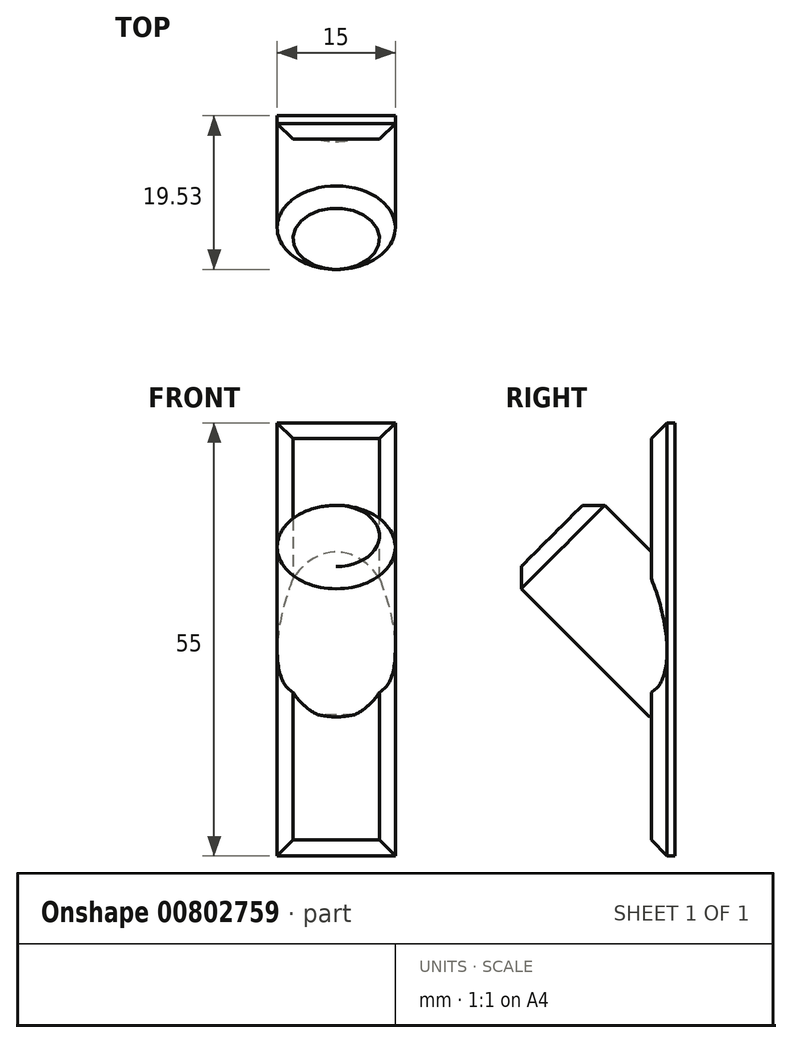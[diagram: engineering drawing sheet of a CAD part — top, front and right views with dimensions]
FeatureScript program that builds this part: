
annotation { "Feature Type Name" : "Feature", "Feature Type Description" : "" }
export const myFeature = defineFeature(function(context is Context, id is Id, definition is map)
    precondition{}
    {
        {
            var Q0;
            Q0=qCreatedBy(makeId("Front.planeOp"),FACE);
            var sketch = newSketch(context, id + "F0", { "sketchPlane" : qUnion([Q0])});
            skLineSegment(sketch, "E0.bottom", {"start": v(-7.5, 30) * mm, "end": v(7.5, 30) * mm});
            skLineSegment(sketch, "E0.top", {"start": v(-7.5, -25) * mm, "end": v(7.5, -25) * mm});
            skLineSegment(sketch, "E0.left", {"start": v(-7.5, 30) * mm, "end": v(-7.5, -25) * mm});
            skLineSegment(sketch, "E0.right", {"start": v(7.5, 30) * mm, "end": v(7.5, -25) * mm});
            skSolve(sketch);
        }
        {
            var Q0;
            Q0=qSketchRegion(id+"F0",true);
            extrude(context, id + "F1", {"entities" : qUnion([Q0]), "depth" : 3 * mm, "offsetDistance" : 25 * mm});
        }
        {
            var Q0;
            Q0=makeQuery(id+"F1.opExtrude","CAP_FACE",FACE,{"disambiguationData":[OSD([sQuery(id+"F0.wireOp",EDGE,"E0.bottom"),sQuery(id+"F0.wireOp",EDGE,"E0.top"),sQuery(id+"F0.wireOp",EDGE,"E0.left"),sQuery(id+"F0.wireOp",EDGE,"E0.right")])],"isStart":false});
            var sketch = newSketch(context, id + "F2", { "sketchPlane" : qUnion([Q0])});
            skLineSegment(sketch, "E1", {"start": v(-6.42, 0) * mm, "end": v(9.7, 0) * mm, "construction": true});
            skSolve(sketch);
        }
        {
            var Q0;
            Q0=qCreatedBy(makeId("Origin.pointOp"),VERTEX);
            var Q1;
            Q1=sQuery(id+"F2.wireOp",EDGE,"E1");
            cPlane(context, id + "F3", {"entities" : qUnion([Q0, Q1]), "cplaneType" : CPlaneType.LINE_ANGLE, "offset" : 25 * mm, "angle" : 45 * degree, "width" : 150 * mm, "height" : 150 * mm});
        }
        {
            var Q0;
            Q0=qCreatedBy(id+"F3.planeOp",FACE);
            var sketch = newSketch(context, id + "F4", { "sketchPlane" : qUnion([Q0])});
            skCircle(sketch, "E2", {"center": v(0, 0) * mm, "radius": 7.5 * mm});
            skSolve(sketch);
        }
        {
            var Q0;
            Q0=qSketchRegion(id+"F4",true);
            extrude(context, id + "F5", {"entities" : qUnion([Q0]), "operationType" : NewBodyOperationType.ADD, "depth" : 20 * mm, "offsetDistance" : 25 * mm, "hasSecondDirection" : true, "secondDirectionOppositeDirection" : true, "secondDirectionDepth" : 5 * mm});
        }
        {
            var Q0;
            {var subQ0=sQuery(id+"F0.wireOp",EDGE,"E0.bottom");var subQ1=sQuery(id+"F0.wireOp",EDGE,"E0.left");Q0=makeQuery(id+"F5.boolean.opBoolean","SPLIT",EDGE,{"disambiguationData":[TD([makeQuery(id+"F1.opExtrude","SWEPT_FACE",FACE,{"disambiguationData":[OSD([subQ0])]})])],"derivedFrom":makeQuery(id+"F1.opExtrude","CAP_EDGE",EDGE,{"disambiguationData":[OSD([subQ1])],"isStart":false})});}
            var Q1;
            Q1=makeQuery(id+"F5.opExtrude","CAP_EDGE",EDGE,{"disambiguationData":[OSD([sQuery(id+"F4.wireOp",EDGE,"E2")])],"isStart":false});
            var Q2;
            Q2=makeQuery(id+"F1.opExtrude","CAP_EDGE",EDGE,{"disambiguationData":[OSD([sQuery(id+"F0.wireOp",EDGE,"E0.bottom")])],"isStart":false});
            var Q3;
            Q3=makeQuery(id+"F1.opExtrude","CAP_EDGE",EDGE,{"disambiguationData":[OSD([sQuery(id+"F0.wireOp",EDGE,"E0.top")])],"isStart":false});
            var Q4;
            {var subQ0=sQuery(id+"F0.wireOp",EDGE,"E0.bottom");var subQ1=sQuery(id+"F0.wireOp",EDGE,"E0.right");Q4=makeQuery(id+"F5.boolean.opBoolean","SPLIT",EDGE,{"disambiguationData":[TD([makeQuery(id+"F1.opExtrude","SWEPT_FACE",FACE,{"disambiguationData":[OSD([subQ0])]})])],"derivedFrom":makeQuery(id+"F1.opExtrude","CAP_EDGE",EDGE,{"disambiguationData":[OSD([subQ1])],"isStart":false})});}
            chamfer(context, id + "F6", {"entities" : qUnion([Q0, Q1, Q2, Q3, Q4]), "width" : 2 * mm, "tangentPropagation" : true});
        }
        {
            var Q0;
            Q0=makeQuery(id+"F0.imprint","IMPRINT",FACE,{"disambiguationData":[TD([[makeQuery(id+"F0.imprint","IMPRINT",EDGE,{"derivedFrom":sQuery(id+"F0.wireOp",EDGE,"E0.bottom")}),-1.0]])]});
            extrude(context, id + "F7", {"entities" : qUnion([Q0]), "operationType" : NewBodyOperationType.REMOVE, "oppositeDirection" : true, "depth" : 25 * mm, "offsetDistance" : 25 * mm});
        }
    });
